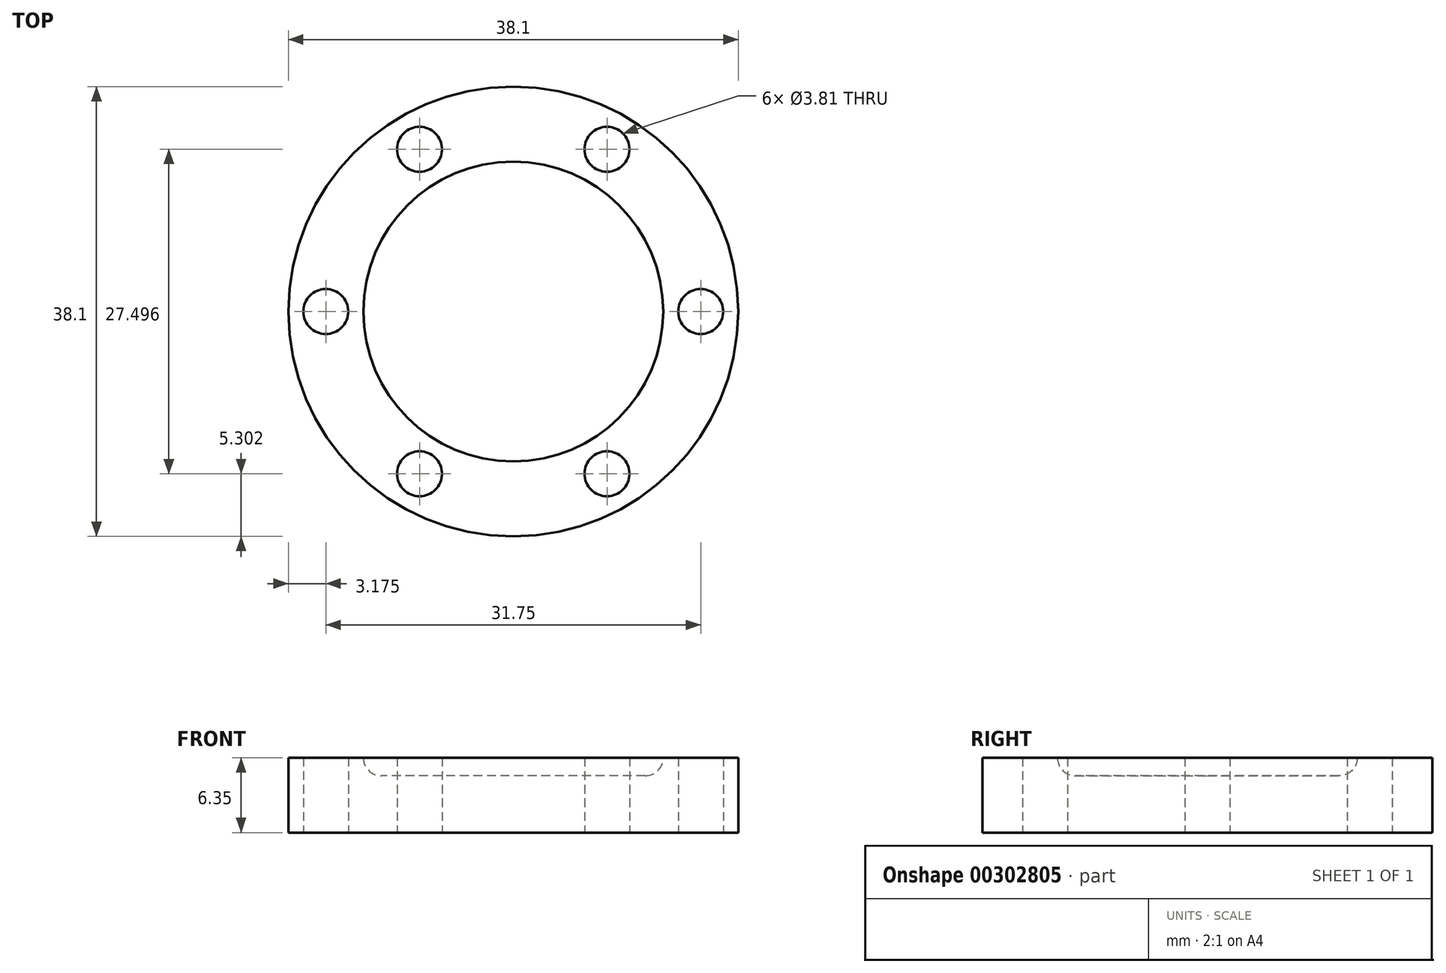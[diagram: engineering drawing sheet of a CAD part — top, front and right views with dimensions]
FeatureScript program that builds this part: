
annotation { "Feature Type Name" : "Feature", "Feature Type Description" : "" }
export const myFeature = defineFeature(function(context is Context, id is Id, definition is map)
    precondition{}
    {
        {
            var Q0;
            Q0=qCreatedBy(makeId("Top.planeOp"),FACE);
            var sketch = newSketch(context, id + "F0", { "sketchPlane" : qUnion([Q0])});
            skCircle(sketch, "E0", {"center": v(0, 0) * mm, "radius": 19.05 * mm});
            skPoint(sketch, "E1", {"position": v(15.88, 0) * mm});
            skCircle(sketch, "E2.cCircle", {"center": v(0, 0) * mm, "radius": 15.88 * mm, "construction": true});
            skLineSegment(sketch, "E2.0", {"start": v(15.88, 0) * mm, "end": v(7.94, -13.75) * mm, "construction": true});
            skLineSegment(sketch, "E2.1", {"start": v(7.94, -13.75) * mm, "end": v(-7.94, -13.75) * mm, "construction": true});
            skLineSegment(sketch, "E2.2", {"start": v(-7.94, -13.75) * mm, "end": v(-15.88, 0) * mm, "construction": true});
            skLineSegment(sketch, "E2.3", {"start": v(-15.88, 0) * mm, "end": v(-7.94, 13.75) * mm, "construction": true});
            skLineSegment(sketch, "E2.4", {"start": v(-7.94, 13.75) * mm, "end": v(7.94, 13.75) * mm, "construction": true});
            skLineSegment(sketch, "E2.5", {"start": v(7.94, 13.75) * mm, "end": v(15.88, 0) * mm, "construction": true});
            skPoint(sketch, "E3", {"position": v(-7.94, 13.75) * mm});
            skPoint(sketch, "E4", {"position": v(7.94, 13.75) * mm});
            skPoint(sketch, "E5", {"position": v(-15.88, 0) * mm});
            skPoint(sketch, "E6", {"position": v(-7.94, -13.75) * mm});
            skPoint(sketch, "E7", {"position": v(7.94, -13.75) * mm});
            skSolve(sketch);
        }
        {
            var Q0;
            Q0=makeQuery(id+"F0.imprint","IMPRINT",FACE,{"disambiguationData":[TD([[makeQuery(id+"F0.imprint","IMPRINT",EDGE,{"derivedFrom":sQuery(id+"F0.wireOp",EDGE,"E0")}),1.0]])]});
            extrude(context, id + "F1", {"entities" : qUnion([Q0]), "depth" : 6.35 * mm});
        }
        {
            var Q0;
            Q0=sQuery(id+"F0.wireOp",VERTEX,"E7");
            var Q1;
            Q1=sQuery(id+"F0.wireOp",VERTEX,"E6");
            var Q2;
            Q2=sQuery(id+"F0.wireOp",VERTEX,"E5");
            var Q3;
            Q3=sQuery(id+"F0.wireOp",VERTEX,"E3");
            var Q4;
            Q4=sQuery(id+"F0.wireOp",VERTEX,"E4");
            var Q5;
            Q5=sQuery(id+"F0.wireOp",VERTEX,"E1");
            var Q6;
            Q6=makeQuery(id+"F1.opExtrude","SWEPT_BODY",BODY,{"disambiguationData":[OSD([sQuery(id+"F0.wireOp",EDGE,"E0")])]});
            hole(context, id + "F2", {"style" : HoleStyle.SIMPLE, "endStyle" : HoleEndStyle.THROUGH, "oppositeDirection" : true, "holeDiameter" : 3.8 * mm, "isTappedThrough" : true, "tappedDepth" : 12.7 * mm, "tapClearance" : 3, "locations" : qUnion([Q0, Q1, Q2, Q3, Q4, Q5]), "scope" : qUnion([Q6])});
        }
        {
            var Q0;
            Q0=makeQuery(id+"F1.opExtrude","CAP_FACE",FACE,{"disambiguationData":[OSD([sQuery(id+"F0.wireOp",EDGE,"E0")])],"isStart":false});
            var sketch = newSketch(context, id + "F3", { "sketchPlane" : qUnion([Q0])});
            skCircle(sketch, "E8", {"center": v(0, 0) * mm, "radius": 12.7 * mm});
            skSolve(sketch);
        }
        {
            var Q0;
            Q0=makeQuery(id+"F3.imprint","IMPRINT",FACE,{"disambiguationData":[TD([[makeQuery(id+"F3.imprint","IMPRINT",EDGE,{"derivedFrom":sQuery(id+"F3.wireOp",EDGE,"E8")}),1.0]])]});
            extrude(context, id + "F4", {"entities" : qUnion([Q0]), "operationType" : NewBodyOperationType.REMOVE, "oppositeDirection" : true, "depth" : 1.52 * mm});
        }
        {
            var Q0;
            Q0=makeQuery(id+"F4.boolean.opBoolean","COPY",EDGE,{"derivedFrom":makeQuery(id+"F4.opExtrude","CAP_EDGE",EDGE,{"disambiguationData":[OSD([sQuery(id+"F3.wireOp",EDGE,"E8")])],"isStart":false})});
            fillet(context, id + "F5", {"entities" : qUnion([Q0]), "radius" : 1.52 * mm, "tangentPropagation" : true, "allowEdgeOverflow" : false});
        }
    });
